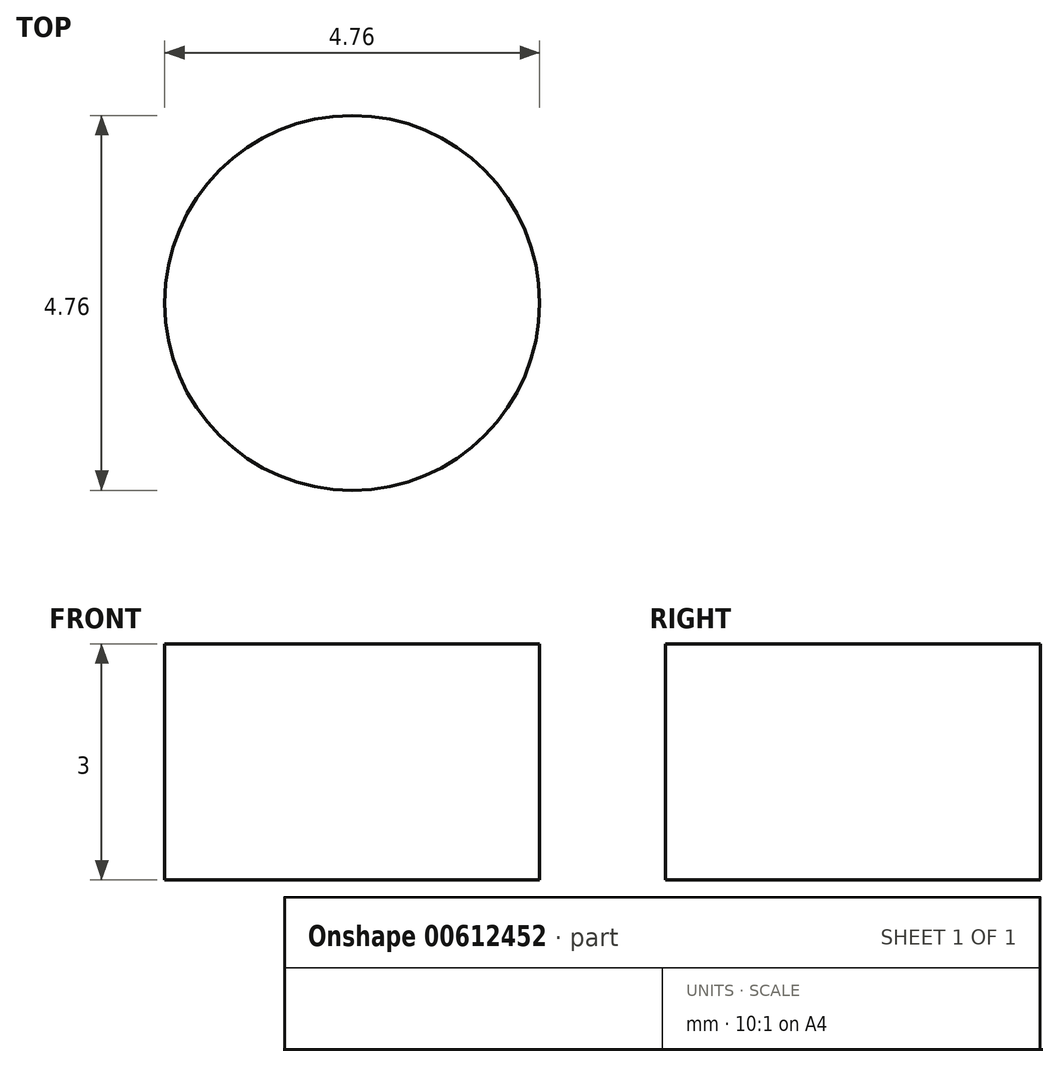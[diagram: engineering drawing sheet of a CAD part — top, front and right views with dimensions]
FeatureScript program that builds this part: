
annotation { "Feature Type Name" : "Feature", "Feature Type Description" : "" }
export const myFeature = defineFeature(function(context is Context, id is Id, definition is map)
    precondition{}
    {
        {
            var Q0;
            Q0=qCreatedBy(makeId("Top.planeOp"),FACE);
            var sketch = newSketch(context, id + "F0", { "sketchPlane" : qUnion([Q0])});
            skLineSegment(sketch, "E0.bottom", {"start": v(0, 0) * mm, "end": v(75, 0) * mm, "construction": true});
            skLineSegment(sketch, "E0.top", {"start": v(0, 75) * mm, "end": v(75, 75) * mm, "construction": true});
            skLineSegment(sketch, "E0.left", {"start": v(0, 0) * mm, "end": v(0, 75) * mm, "construction": true});
            skLineSegment(sketch, "E0.right", {"start": v(75, 0) * mm, "end": v(75, 75) * mm, "construction": true});
            skLineSegment(sketch, "E1", {"start": v(0, 75) * mm, "end": v(75, 0) * mm, "construction": true});
            skCircle(sketch, "E2", {"center": v(37.5, 37.5) * mm, "radius": 2.38 * mm});
            skArc(sketch, "E3", {"start": v(29.31, 74.1) * mm, "mid": v(14.43, 67.06) * mm, "end": v(4, 54.34) * mm});
            skLineSegment(sketch, "E4", {"start": v(29.26, 43.05) * mm, "end": v(32.6, 46.38) * mm});
            skLineSegment(sketch, "E5", {"start": v(32.6, 46.38) * mm, "end": v(28.54, 65.55) * mm});
            skLineSegment(sketch, "E6", {"start": v(29.26, 43.05) * mm, "end": v(9.1, 50.43) * mm});
            skArc(sketch, "E7", {"start": v(28.54, 65.55) * mm, "mid": v(14.33, 63.77) * mm, "end": v(9.1, 50.43) * mm});
            skLineSegment(sketch, "E8", {"start": v(9.6, 45.96) * mm, "end": v(28.3, 35.03) * mm});
            skLineSegment(sketch, "E9", {"start": v(28.3, 35.03) * mm, "end": v(14.35, 18.2) * mm});
            skLineSegment(sketch, "E10", {"start": v(14.35, 18.2) * mm, "end": v(9.6, 45.96) * mm});
            skArc(sketch, "E11.1.0", {"start": v(17.69, 15.72) * mm, "mid": v(26.33, 4.3) * mm, "end": v(40.5, 6.45) * mm});
            skLineSegment(sketch, "E11.1.1", {"start": v(36.8, 27.59) * mm, "end": v(40.5, 6.45) * mm});
            skLineSegment(sketch, "E11.1.2", {"start": v(32.26, 28.8) * mm, "end": v(17.69, 15.72) * mm});
            skLineSegment(sketch, "E11.1.3", {"start": v(36.8, 27.59) * mm, "end": v(32.26, 28.8) * mm});
            skLineSegment(sketch, "E11.1.4", {"start": v(44.24, 30.76) * mm, "end": v(65.79, 27.1) * mm});
            skLineSegment(sketch, "E11.1.5", {"start": v(44.12, 9.11) * mm, "end": v(44.24, 30.76) * mm});
            skLineSegment(sketch, "E11.1.6", {"start": v(65.79, 27.1) * mm, "end": v(44.12, 9.11) * mm});
            skArc(sketch, "E11.2.0", {"start": v(66.27, 31.23) * mm, "mid": v(71.84, 44.43) * mm, "end": v(62.9, 55.62) * mm});
            skLineSegment(sketch, "E11.2.1", {"start": v(46.43, 41.86) * mm, "end": v(62.9, 55.62) * mm});
            skLineSegment(sketch, "E11.2.2", {"start": v(47.65, 37.3) * mm, "end": v(66.27, 31.23) * mm});
            skLineSegment(sketch, "E11.2.3", {"start": v(46.43, 41.86) * mm, "end": v(47.65, 37.3) * mm});
            skLineSegment(sketch, "E11.2.4", {"start": v(39.97, 46.7) * mm, "end": v(32.37, 67.2) * mm});
            skLineSegment(sketch, "E11.2.5", {"start": v(58.77, 57.43) * mm, "end": v(39.97, 46.7) * mm});
            skLineSegment(sketch, "E11.2.6", {"start": v(32.37, 67.2) * mm, "end": v(58.77, 57.43) * mm});
            skPoint(sketch, "E12.endSnap0", {"position": v(0, 37.5) * mm});
            skLineSegment(sketch, "E13", {"start": v(4, 54.34) * mm, "end": v(9.9, 12.11) * mm});
            skLineSegment(sketch, "E14.1.0", {"start": v(39.67, 0.06) * mm, "end": v(73.29, 26.3) * mm});
            skLineSegment(sketch, "E14.2.0", {"start": v(68.83, 58.1) * mm, "end": v(29.31, 74.1) * mm});
            skArc(sketch, "E15.trimOffspring", {"start": v(9.9, 12.11) * mm, "mid": v(23.43, 2.74) * mm, "end": v(39.67, 0.06) * mm});
            skArc(sketch, "E16.trimOffspring", {"start": v(73.29, 26.3) * mm, "mid": v(74.64, 42.7) * mm, "end": v(68.83, 58.1) * mm});
            skSolve(sketch);
        }
        {
            var Q0;
            Q0=makeQuery(id+"F0.imprint","IMPRINT",FACE,{"disambiguationData":[TD([[makeQuery(id+"F0.imprint","IMPRINT",EDGE,{"derivedFrom":sQuery(id+"F0.wireOp",EDGE,"E2")}),1.0]])]});
            extrude(context, id + "F1", {"entities" : qUnion([Q0]), "depth" : 3 * mm, "offsetDistance" : 25 * mm});
        }
    });
